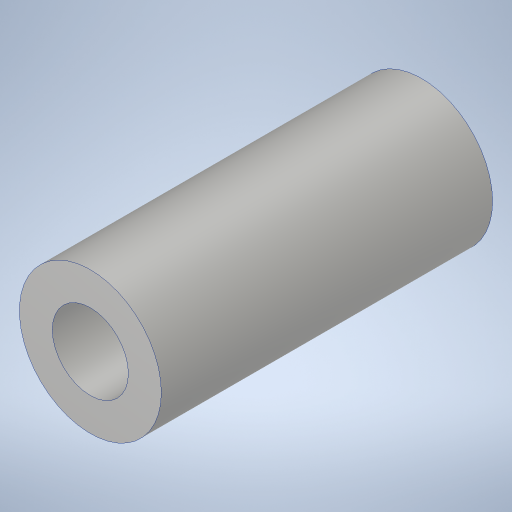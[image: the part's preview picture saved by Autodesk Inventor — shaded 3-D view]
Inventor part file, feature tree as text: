
AUTODESK INVENTOR PART (.ipt)
format: ipt  version: 2023.4 (Build 274418000, 418)  size: 218,112 bytes
history: native  units: in
note: dims shown in document units (in); Inventor stores cm internally (conversion verified against a paired STEP export)
features: extrude x1, sketch x1
ambient origin geometry x8: Origin, YZ Plane, XZ Plane, XY Plane, X Axis, Y Axis, Z Axis, Center Point
bodies: Solid1 (feature_tree)
feature tree (2):
  extrude  "Extrusion1"  Depth=0.875in
  sketch  "Sketch1"  dims[d0=0.375in d1=0.201in d2=0.875in d3=0.0in]
